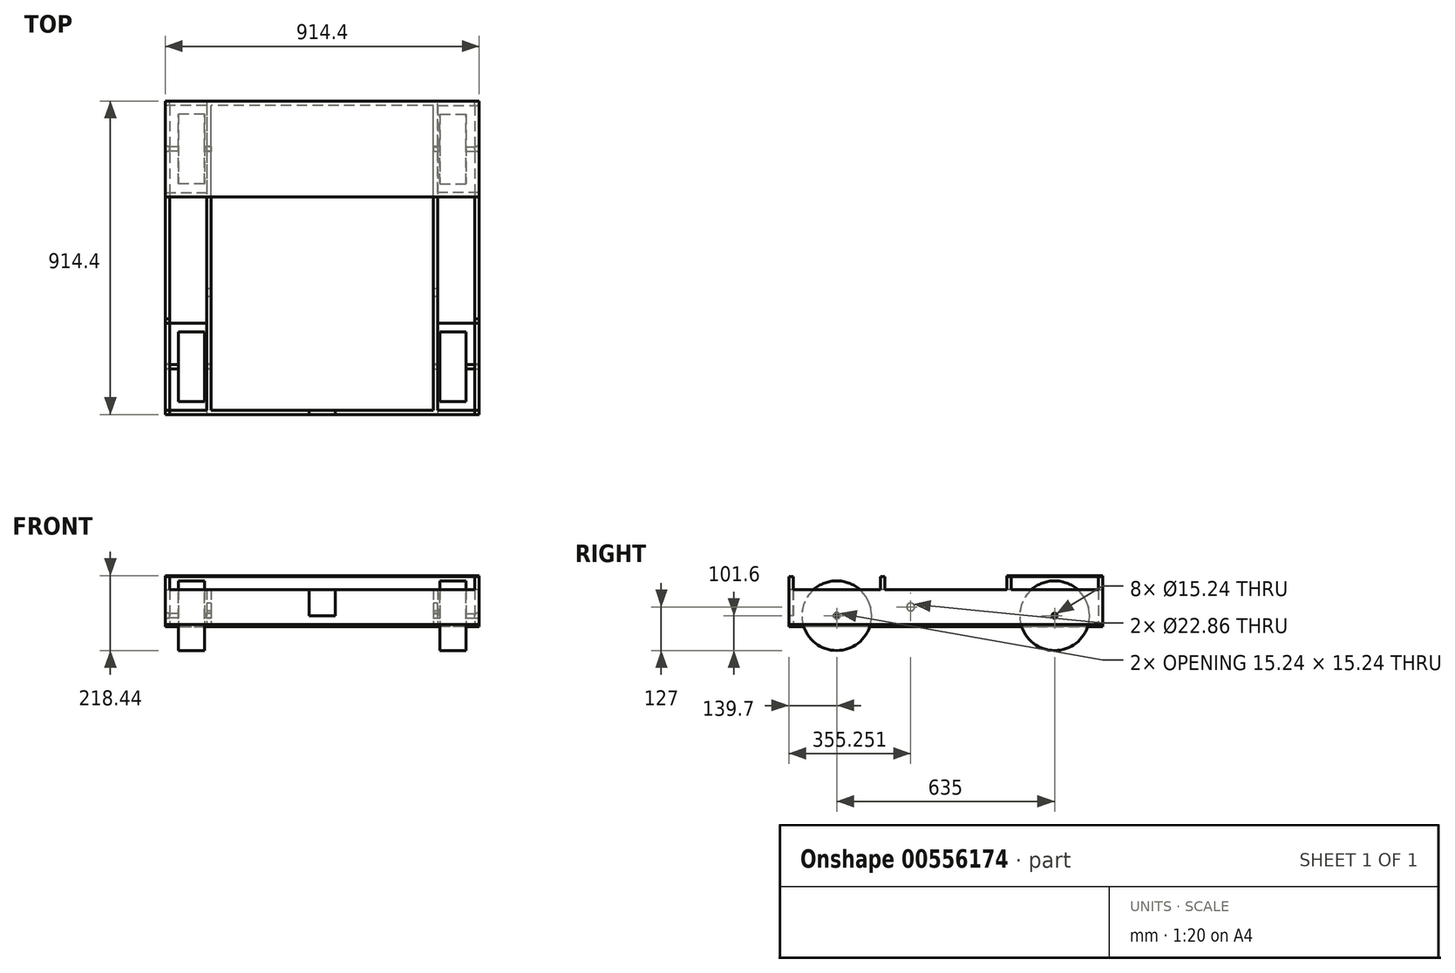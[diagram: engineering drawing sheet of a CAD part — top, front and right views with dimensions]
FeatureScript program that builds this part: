
annotation { "Feature Type Name" : "Feature", "Feature Type Description" : "" }
export const myFeature = defineFeature(function(context is Context, id is Id, definition is map)
    precondition{}
    {
        {
            var Q0;
            Q0=qCreatedBy(makeId("Top.planeOp"),FACE);
            var sketch = newSketch(context, id + "F0", { "sketchPlane" : qUnion([Q0])});
            skLineSegment(sketch, "E0", {"start": v(0, 457.2) * mm, "end": v(0, -457.2) * mm, "construction": true});
            skLineSegment(sketch, "E1", {"start": v(0, 444.5) * mm, "end": v(-444.5, 444.5) * mm});
            skLineSegment(sketch, "E2.MirrorCS", {"start": v(-254, -444.5) * mm, "end": v(-444.5, -444.5) * mm});
            skLineSegment(sketch, "E3.MirrorCS", {"start": v(0, 444.5) * mm, "end": v(444.5, 444.5) * mm});
            skLineSegment(sketch, "E4.MirrorCS", {"start": v(114.3, -444.5) * mm, "end": v(444.5, -444.5) * mm});
            skLineSegment(sketch, "E5", {"start": v(-457.2, 444.5) * mm, "end": v(-457.2, -444.5) * mm});
            skLineSegment(sketch, "E6", {"start": v(-444.5, 444.5) * mm, "end": v(-444.5, -444.5) * mm});
            skLineSegment(sketch, "E7.MirrorCS", {"start": v(444.5, 444.5) * mm, "end": v(444.5, -444.5) * mm});
            skLineSegment(sketch, "E8.MirrorCS", {"start": v(457.2, 444.5) * mm, "end": v(457.2, -444.5) * mm});
            skPoint(sketch, "E9.orphan", {"position": v(0, -444.5) * mm});
            skLineSegment(sketch, "E10.trimOffspring", {"start": v(-241.3, -457.2) * mm, "end": v(-457.2, -457.2) * mm});
            skLineSegment(sketch, "E11", {"start": v(-254, -444.5) * mm, "end": v(114.3, -444.5) * mm});
            skLineSegment(sketch, "E12", {"start": v(-38.1, -457.2) * mm, "end": v(-241.3, -457.2) * mm});
            skLineSegment(sketch, "E13", {"start": v(-457.2, 444.5) * mm, "end": v(-457.2, 457.2) * mm});
            skLineSegment(sketch, "E14", {"start": v(-457.2, -444.5) * mm, "end": v(-457.2, -457.2) * mm});
            skLineSegment(sketch, "E15", {"start": v(457.2, -444.5) * mm, "end": v(457.2, -457.2) * mm});
            skLineSegment(sketch, "E16", {"start": v(457.2, 444.5) * mm, "end": v(457.2, 457.2) * mm});
            skLineSegment(sketch, "E17.trimOffspring", {"start": v(457.2, 457.2) * mm, "end": v(-457.2, 457.2) * mm});
            skLineSegment(sketch, "E18.trimOffspring", {"start": v(457.2, -457.2) * mm, "end": v(-38.1, -457.2) * mm});
            skLineSegment(sketch, "E19", {"start": v(-336.55, 444.5) * mm, "end": v(-336.55, -444.5) * mm});
            skLineSegment(sketch, "E20", {"start": v(-323.85, -444.5) * mm, "end": v(-323.85, 444.5) * mm});
            skLineSegment(sketch, "E21.MirrorCS", {"start": v(336.55, 444.5) * mm, "end": v(336.55, -444.5) * mm});
            skLineSegment(sketch, "E22.MirrorCS", {"start": v(323.85, -444.5) * mm, "end": v(323.85, 444.5) * mm});
            skLineSegment(sketch, "E23", {"start": v(-457.2, 444.5) * mm, "end": v(-444.5, 444.5) * mm});
            skLineSegment(sketch, "E24", {"start": v(-336.55, 444.5) * mm, "end": v(-323.85, 444.5) * mm});
            skLineSegment(sketch, "E25", {"start": v(323.85, 444.5) * mm, "end": v(336.55, 444.5) * mm});
            skLineSegment(sketch, "E26", {"start": v(444.5, 444.5) * mm, "end": v(457.2, 444.5) * mm});
            skLineSegment(sketch, "E27", {"start": v(444.5, -444.5) * mm, "end": v(457.2, -444.5) * mm});
            skLineSegment(sketch, "E28", {"start": v(-444.5, -444.5) * mm, "end": v(-457.2, -444.5) * mm});
            skSolve(sketch);
        }
        {
            var Q0;
            Q0=makeQuery(id+"F0.imprint","IMPRINT",FACE,{"disambiguationData":[TD([[makeQuery(id+"F0.imprint","IMPRINT",EDGE,{"derivedFrom":sQuery(id+"F0.wireOp",EDGE,"E5")}),1.0]])]});
            var Q1;
            {var subQ0=sQuery(id+"F0.wireOp",EDGE,"E19");Q1=makeQuery(id+"F0.imprint","IMPRINT",FACE,{"disambiguationData":[TD([[makeQuery(id+"F0.imprint","IMPRINT",EDGE,{"derivedFrom":subQ0}),1.0]])]});}
            var Q2;
            Q2=makeQuery(id+"F0.imprint","IMPRINT",FACE,{"disambiguationData":[TD([[makeQuery(id+"F0.imprint","IMPRINT",EDGE,{"derivedFrom":sQuery(id+"F0.wireOp",EDGE,"E13")}),-1.0]])]});
            var Q3;
            {var subQ0=sQuery(id+"F0.wireOp",EDGE,"E21.MirrorCS");Q3=makeQuery(id+"F0.imprint","IMPRINT",FACE,{"disambiguationData":[TD([[makeQuery(id+"F0.imprint","IMPRINT",EDGE,{"derivedFrom":subQ0}),-1.0]])]});}
            var Q4;
            Q4=makeQuery(id+"F0.imprint","IMPRINT",FACE,{"disambiguationData":[TD([[makeQuery(id+"F0.imprint","IMPRINT",EDGE,{"derivedFrom":sQuery(id+"F0.wireOp",EDGE,"E7.MirrorCS")}),1.0]])]});
            var Q5;
            Q5=makeQuery(id+"F0.imprint","IMPRINT",FACE,{"disambiguationData":[TD([[makeQuery(id+"F0.imprint","IMPRINT",EDGE,{"derivedFrom":sQuery(id+"F0.wireOp",EDGE,"E10.trimOffspring")}),-1.0]])]});
            extrude(context, id + "F1", {"entities" : qUnion([Q0, Q1, Q2, Q3, Q4, Q5]), "depth" : 76.2 * mm, "offsetDistance" : 25.4 * mm, "hasSecondDirection" : true, "secondDirectionOppositeDirection" : true, "secondDirectionDepth" : 25.4 * mm});
        }
        {
            var Q0;
            Q0=makeQuery(id+"F1.opExtrude","SWEPT_FACE",FACE,{"disambiguationData":[OSD([sQuery(id+"F0.wireOp",EDGE,"E7.MirrorCS")])]});
            var sketch = newSketch(context, id + "F2", { "sketchPlane" : qUnion([Q0])});
            skLineSegment(sketch, "E29", {"start": v(-444.5, 0) * mm, "end": v(444.5, 0) * mm, "construction": true});
            skCircle(sketch, "E30", {"center": v(-317.5, 0) * mm, "radius": 7.62 * mm});
            skLineSegment(sketch, "E31", {"start": v(0, 0) * mm, "end": v(0, 76.2) * mm, "construction": true});
            skCircle(sketch, "E32.MirrorC", {"center": v(317.5, 0) * mm, "radius": 7.62 * mm});
            skSolve(sketch);
        }
        {
            var Q0;
            Q0 = qSketchRegion(id + "F2", true);
            extrude(context, id + "F3", {"entities" : qUnion([Q0]), "operationType" : NewBodyOperationType.REMOVE, "endBound" : BoundingType.THROUGH_ALL, "oppositeDirection" : true, "depth" : 38.1 * mm, "offsetDistance" : 25.4 * mm, "hasSecondDirection" : true, "secondDirectionBound" : SecondDirectionBoundingType.THROUGH_ALL, "secondDirectionOppositeDirection" : false, "secondDirectionDepth" : 25.4 * mm});
        }
        {
            var Q0;
            Q0=qCreatedBy(makeId("Top.planeOp"),FACE);
            var sketch = newSketch(context, id + "F4", { "sketchPlane" : qUnion([Q0])});
            skLineSegment(sketch, "E33.bottom", {"start": v(-419.1, 419.1) * mm, "end": v(-342.9, 419.1) * mm});
            skLineSegment(sketch, "E33.top", {"start": v(-419.1, 317.5) * mm, "end": v(-342.9, 317.5) * mm});
            skLineSegment(sketch, "E33.left", {"start": v(-419.1, 419.1) * mm, "end": v(-419.1, 317.5) * mm});
            skLineSegment(sketch, "E33.right", {"start": v(-342.9, 419.1) * mm, "end": v(-342.9, 323.85) * mm});
            skLineSegment(sketch, "E34.bottom", {"start": v(-342.9, 317.5) * mm, "end": v(-323.85, 317.5) * mm});
            skLineSegment(sketch, "E34.top", {"start": v(-342.9, 323.85) * mm, "end": v(-323.85, 323.85) * mm});
            skLineSegment(sketch, "E34.right", {"start": v(-323.85, 317.5) * mm, "end": v(-323.85, 323.85) * mm});
            skPoint(sketch, "E35", {"position": v(-323.85, 320.68) * mm});
            skLineSegment(sketch, "E36", {"start": v(-419.1, 317.5) * mm, "end": v(-457.2, 317.5) * mm});
            skLineSegment(sketch, "E37", {"start": v(-457.2, 317.5) * mm, "end": v(-457.2, 323.85) * mm});
            skLineSegment(sketch, "E38", {"start": v(-457.2, 323.85) * mm, "end": v(-419.1, 323.85) * mm});
            skLineSegment(sketch, "E39", {"start": v(-342.9, 317.5) * mm, "end": v(-342.9, 323.85) * mm});
            skLineSegment(sketch, "E40.bottom", {"start": v(-431.8, 323.85) * mm, "end": v(-425.45, 323.85) * mm});
            skLineSegment(sketch, "E40.top", {"start": v(-431.8, 342.9) * mm, "end": v(-425.45, 342.9) * mm});
            skLineSegment(sketch, "E40.left", {"start": v(-431.8, 323.85) * mm, "end": v(-431.8, 342.9) * mm});
            skLineSegment(sketch, "E40.right", {"start": v(-425.45, 323.85) * mm, "end": v(-425.45, 342.9) * mm});
            skSolve(sketch);
        }
        {
            var Q0;
            {var subQ3=sQuery(id+"F4.wireOp",EDGE,"E33.bottom");Q0=makeQuery(id+"F4.imprint","IMPRINT",FACE,{"disambiguationData":[TD([[makeQuery(id+"F4.imprint","IMPRINT",EDGE,{"derivedFrom":subQ3}),-1.0]])]});}
            var Q1;
            Q1=makeQuery(id+"F4.imprint","IMPRINT",FACE,{"disambiguationData":[TD([[makeQuery(id+"F4.imprint","IMPRINT",EDGE,{"derivedFrom":sQuery(id+"F4.wireOp",EDGE,"E34.bottom")}),1.0]])]});
            var Q2;
            {var subQ0=sQuery(id+"F4.wireOp",EDGE,"E36");Q2=makeQuery(id+"F4.imprint","IMPRINT",FACE,{"disambiguationData":[TD([[makeQuery(id+"F4.imprint","IMPRINT",EDGE,{"derivedFrom":subQ0}),-1.0]])]});}
            var Q3;
            Q3=makeQuery(id+"F4.imprint","IMPRINT",FACE,{"disambiguationData":[TD([[makeQuery(id+"F4.imprint","IMPRINT",EDGE,{"derivedFrom":sQuery(id+"F4.wireOp",EDGE,"E40.bottom")}),1.0]])]});
            var Q4;
            Q4=sQuery(id+"F4.wireOp",EDGE,"E33.top");
            revolve(context, id + "F5", {"entities" : qUnion([Q0, Q1, Q2, Q3]), "axis" : qUnion([Q4]), "revolveType" : RevolveType.FULL});
        }
        {
            var Q0;
            Q0=makeQuery(id+"F5.opRevolve","SWEPT_BODY",BODY,{"disambiguationData":[OSD([sQuery(id+"F4.wireOp",EDGE,"E33.bottom"),sQuery(id+"F4.wireOp",EDGE,"E33.top"),sQuery(id+"F4.wireOp",EDGE,"E33.left"),sQuery(id+"F4.wireOp",EDGE,"E33.right"),sQuery(id+"F4.wireOp",EDGE,"E34.bottom"),sQuery(id+"F4.wireOp",EDGE,"E34.top"),sQuery(id+"F4.wireOp",EDGE,"E34.right")])]});
            var Q1;
            Q1=qCreatedBy(makeId("Right.planeOp"),FACE);
            mirror(context, id + "F6", {"entities" : qUnion([Q0]), "mirrorPlane" : qUnion([Q1])});
        }
        {
            var Q0;
            Q0=makeQuery(id+"F5.opRevolve","SWEPT_BODY",BODY,{"disambiguationData":[OSD([sQuery(id+"F4.wireOp",EDGE,"E33.bottom"),sQuery(id+"F4.wireOp",EDGE,"E33.top"),sQuery(id+"F4.wireOp",EDGE,"E33.left"),sQuery(id+"F4.wireOp",EDGE,"E33.right"),sQuery(id+"F4.wireOp",EDGE,"E34.bottom"),sQuery(id+"F4.wireOp",EDGE,"E34.top"),sQuery(id+"F4.wireOp",EDGE,"E34.right")])]});
            var Q1;
            Q1=makeQuery(id+"F6.opPattern","COPY",BODY,{"derivedFrom":makeQuery(id+"F5.opRevolve","SWEPT_BODY",BODY,{"disambiguationData":[OSD([sQuery(id+"F4.wireOp",EDGE,"E33.bottom"),sQuery(id+"F4.wireOp",EDGE,"E33.top"),sQuery(id+"F4.wireOp",EDGE,"E33.left"),sQuery(id+"F4.wireOp",EDGE,"E33.right"),sQuery(id+"F4.wireOp",EDGE,"E34.bottom"),sQuery(id+"F4.wireOp",EDGE,"E34.top"),sQuery(id+"F4.wireOp",EDGE,"E34.right")])]}),"instanceName":"1"});
            var Q2;
            Q2=qCreatedBy(makeId("Front.planeOp"),FACE);
            mirror(context, id + "F7", {"entities" : qUnion([Q0, Q1]), "mirrorPlane" : qUnion([Q2])});
        }
        {
            var Q0;
            Q0=makeQuery(id+"F1.opExtrude","CAP_FACE",FACE,{"disambiguationData":[OSD([sQuery(id+"F0.wireOp",EDGE,"E1"),sQuery(id+"F0.wireOp",EDGE,"E2.MirrorCS"),sQuery(id+"F0.wireOp",EDGE,"E3.MirrorCS"),sQuery(id+"F0.wireOp",EDGE,"E4.MirrorCS"),sQuery(id+"F0.wireOp",EDGE,"E5"),sQuery(id+"F0.wireOp",EDGE,"E6"),sQuery(id+"F0.wireOp",EDGE,"E7.MirrorCS"),sQuery(id+"F0.wireOp",EDGE,"E8.MirrorCS"),sQuery(id+"F0.wireOp",EDGE,"E10.trimOffspring"),sQuery(id+"F0.wireOp",EDGE,"E11"),sQuery(id+"F0.wireOp",EDGE,"E12"),sQuery(id+"F0.wireOp",EDGE,"E13"),sQuery(id+"F0.wireOp",EDGE,"E14"),sQuery(id+"F0.wireOp",EDGE,"E15"),sQuery(id+"F0.wireOp",EDGE,"E16"),sQuery(id+"F0.wireOp",EDGE,"E17.trimOffspring"),sQuery(id+"F0.wireOp",EDGE,"E18.trimOffspring")])],"isStart":false});
            var sketch = newSketch(context, id + "F8", { "sketchPlane" : qUnion([Q0])});
            skLineSegment(sketch, "E41.bottom", {"start": v(-444.5, 444.5) * mm, "end": v(-457.2, 444.5) * mm});
            skLineSegment(sketch, "E41.top", {"start": v(-444.5, 457.2) * mm, "end": v(-457.2, 457.2) * mm});
            skLineSegment(sketch, "E41.left", {"start": v(-444.5, 444.5) * mm, "end": v(-444.5, 457.2) * mm});
            skLineSegment(sketch, "E41.right", {"start": v(-457.2, 444.5) * mm, "end": v(-457.2, 457.2) * mm});
            skLineSegment(sketch, "E42", {"start": v(-444.5, 0) * mm, "end": v(444.5, 0) * mm, "construction": true});
            skLineSegment(sketch, "E43", {"start": v(-457.2, 444.5) * mm, "end": v(-457.2, 0) * mm, "construction": true});
            skLineSegment(sketch, "E44.bottom", {"start": v(-457.2, 190.5) * mm, "end": v(-444.5, 190.5) * mm});
            skLineSegment(sketch, "E44.top", {"start": v(-457.2, 177.8) * mm, "end": v(-444.5, 177.8) * mm});
            skLineSegment(sketch, "E44.left", {"start": v(-457.2, 190.5) * mm, "end": v(-457.2, 177.8) * mm});
            skLineSegment(sketch, "E44.right", {"start": v(-444.5, 190.5) * mm, "end": v(-444.5, 177.8) * mm});
            skLineSegment(sketch, "E45.MirrorCS", {"start": v(457.2, 444.5) * mm, "end": v(457.2, 457.2) * mm});
            skLineSegment(sketch, "E46.MirrorCS", {"start": v(444.5, 444.5) * mm, "end": v(444.5, 457.2) * mm});
            skLineSegment(sketch, "E47.MirrorCS", {"start": v(444.5, 457.2) * mm, "end": v(457.2, 457.2) * mm});
            skLineSegment(sketch, "E48.MirrorCS", {"start": v(444.5, 444.5) * mm, "end": v(457.2, 444.5) * mm});
            skLineSegment(sketch, "E49.MirrorCS", {"start": v(457.2, 190.5) * mm, "end": v(444.5, 190.5) * mm});
            skLineSegment(sketch, "E50.MirrorCS", {"start": v(457.2, 177.8) * mm, "end": v(444.5, 177.8) * mm});
            skLineSegment(sketch, "E51.MirrorCS", {"start": v(444.5, 190.5) * mm, "end": v(444.5, 177.8) * mm});
            skLineSegment(sketch, "E52.MirrorCS", {"start": v(457.2, 190.5) * mm, "end": v(457.2, 177.8) * mm});
            skLineSegment(sketch, "E53.MirrorCS", {"start": v(444.5, -444.5) * mm, "end": v(457.2, -444.5) * mm});
            skLineSegment(sketch, "E54.MirrorCS", {"start": v(-444.5, -444.5) * mm, "end": v(-457.2, -444.5) * mm});
            skLineSegment(sketch, "E55.MirrorCS", {"start": v(-444.5, -457.2) * mm, "end": v(-457.2, -457.2) * mm});
            skLineSegment(sketch, "E56.MirrorCS", {"start": v(-444.5, -444.5) * mm, "end": v(-444.5, -457.2) * mm});
            skLineSegment(sketch, "E57.MirrorCS", {"start": v(-457.2, -444.5) * mm, "end": v(-457.2, -457.2) * mm});
            skLineSegment(sketch, "E58.MirrorCS", {"start": v(457.2, -444.5) * mm, "end": v(457.2, -457.2) * mm});
            skLineSegment(sketch, "E59.MirrorCS", {"start": v(444.5, -444.5) * mm, "end": v(444.5, -457.2) * mm});
            skLineSegment(sketch, "E60.MirrorCS", {"start": v(457.2, -190.5) * mm, "end": v(444.5, -190.5) * mm});
            skLineSegment(sketch, "E61.MirrorCS", {"start": v(457.2, -177.8) * mm, "end": v(444.5, -177.8) * mm});
            skLineSegment(sketch, "E62.MirrorCS", {"start": v(444.5, -190.5) * mm, "end": v(444.5, -177.8) * mm});
            skLineSegment(sketch, "E63.MirrorCS", {"start": v(457.2, -190.5) * mm, "end": v(457.2, -177.8) * mm});
            skLineSegment(sketch, "E64.MirrorCS", {"start": v(-457.2, -190.5) * mm, "end": v(-444.5, -190.5) * mm});
            skLineSegment(sketch, "E65.MirrorCS", {"start": v(-444.5, -190.5) * mm, "end": v(-444.5, -177.8) * mm});
            skLineSegment(sketch, "E66.MirrorCS", {"start": v(-457.2, -177.8) * mm, "end": v(-444.5, -177.8) * mm});
            skLineSegment(sketch, "E67.MirrorCS", {"start": v(-457.2, -190.5) * mm, "end": v(-457.2, -177.8) * mm});
            skLineSegment(sketch, "E68.MirrorCS", {"start": v(444.5, -457.2) * mm, "end": v(457.2, -457.2) * mm});
            skSolve(sketch);
        }
        {
            var Q0;
            Q0 = qSketchRegion(id + "F8", true);
            extrude(context, id + "F9", {"entities" : qUnion([Q0]), "operationType" : NewBodyOperationType.ADD, "depth" : 38.1 * mm, "offsetDistance" : 25.4 * mm});
        }
        {
            var Q0;
            Q0=makeQuery(id+"F9.opExtrude","CAP_FACE",FACE,{"disambiguationData":[OSD([sQuery(id+"F8.wireOp",EDGE,"E41.bottom"),sQuery(id+"F8.wireOp",EDGE,"E41.top"),sQuery(id+"F8.wireOp",EDGE,"E41.left"),sQuery(id+"F8.wireOp",EDGE,"E41.right")])],"isStart":false});
            var sketch = newSketch(context, id + "F10", { "sketchPlane" : qUnion([Q0])});
            skLineSegment(sketch, "E69.bottom", {"start": v(-457.2, 457.2) * mm, "end": v(457.2, 457.2) * mm});
            skLineSegment(sketch, "E69.top", {"start": v(-457.2, 177.8) * mm, "end": v(457.2, 177.8) * mm});
            skLineSegment(sketch, "E69.left", {"start": v(-457.2, 457.2) * mm, "end": v(-457.2, 177.8) * mm});
            skLineSegment(sketch, "E69.right", {"start": v(457.2, 457.2) * mm, "end": v(457.2, 177.8) * mm});
            skSolve(sketch);
        }
        {
            var Q0;
            Q0 = qSketchRegion(id + "F10", true);
            extrude(context, id + "F11", {"entities" : qUnion([Q0]), "depth" : 2.54 * mm, "offsetDistance" : 25.4 * mm});
        }
        {
            var Q0;
            Q0=makeQuery(id+"F1.opExtrude","CAP_FACE",FACE,{"disambiguationData":[OSD([sQuery(id+"F0.wireOp",EDGE,"QB7noLBN-PpOc-EJPR-Sd6c-0ypbwZ1Wte7m.bottom"),sQuery(id+"F0.wireOp",EDGE,"QB7noLBN-PpOc-EJPR-Sd6c-0ypbwZ1Wte7m.top"),sQuery(id+"F0.wireOp",EDGE,"QB7noLBN-PpOc-EJPR-Sd6c-0ypbwZ1Wte7m.left"),sQuery(id+"F0.wireOp",EDGE,"QB7noLBN-PpOc-EJPR-Sd6c-0ypbwZ1Wte7m.right"),sQuery(id+"F0.wireOp",EDGE,"PR4ij4Z3-PY9W-TKVm-yz0G-q3J5sclFM2MW"),sQuery(id+"F0.wireOp",EDGE,"E1"),sQuery(id+"F0.wireOp",EDGE,"E2.MirrorCS"),sQuery(id+"F0.wireOp",EDGE,"E3.MirrorCS"),sQuery(id+"F0.wireOp",EDGE,"855b87ce-e732-4e19-91af-ca48fbd712201.MirrorCS"),sQuery(id+"F0.wireOp",EDGE,"E4.MirrorCS"),sQuery(id+"F0.wireOp",EDGE,"E5"),sQuery(id+"F0.wireOp",EDGE,"E6"),sQuery(id+"F0.wireOp",EDGE,"E7.MirrorCS"),sQuery(id+"F0.wireOp",EDGE,"E8.MirrorCS"),sQuery(id+"F0.wireOp",EDGE,"31cbcaf3-3368-42d4-bf1a-20ab076e13b5.trimOffspring"),sQuery(id+"F0.wireOp",EDGE,"ae03b67a-2540-4bec-9181-0f3f2fe8d185.trimOffspring"),sQuery(id+"F0.wireOp",EDGE,"7d0354b2-750d-4ba2-8c9c-4a323621a8be.trimOffspring"),sQuery(id+"F0.wireOp",EDGE,"423b36b6-17ea-44a3-93c2-e0b44851f98a.trimOffspring"),sQuery(id+"F0.wireOp",EDGE,"E10.trimOffspring"),sQuery(id+"F0.wireOp",EDGE,"E11"),sQuery(id+"F0.wireOp",EDGE,"E12")])],"isStart":true});
            var sketch = newSketch(context, id + "F12", { "sketchPlane" : qUnion([Q0])});
            skLineSegment(sketch, "E70", {"start": v(0, -457.2) * mm, "end": v(0, 457.2) * mm, "construction": true});
            skLineSegment(sketch, "E71", {"start": v(-457.2, 0) * mm, "end": v(457.2, 0) * mm, "construction": true});
            skLineSegment(sketch, "E72", {"start": v(-457.2, 0) * mm, "end": v(-457.2, 190.5) * mm});
            skLineSegment(sketch, "E73", {"start": v(-457.2, 190.5) * mm, "end": v(-336.55, 190.5) * mm});
            skLineSegment(sketch, "E74", {"start": v(-336.55, 190.5) * mm, "end": v(-336.55, 457.2) * mm});
            skLineSegment(sketch, "E75", {"start": v(-336.55, 457.2) * mm, "end": v(0, 457.2) * mm});
            skLineSegment(sketch, "E76.MirrorCS", {"start": v(336.55, 457.2) * mm, "end": v(0, 457.2) * mm});
            skLineSegment(sketch, "E77.MirrorCS", {"start": v(457.2, 0) * mm, "end": v(457.2, 190.5) * mm});
            skLineSegment(sketch, "E78.MirrorCS", {"start": v(457.2, 190.5) * mm, "end": v(336.55, 190.5) * mm});
            skLineSegment(sketch, "E79.MirrorCS", {"start": v(336.55, 190.5) * mm, "end": v(336.55, 457.2) * mm});
            skLineSegment(sketch, "E80.MirrorCS", {"start": v(457.2, -190.5) * mm, "end": v(336.55, -190.5) * mm});
            skLineSegment(sketch, "E81.MirrorCS", {"start": v(336.55, -190.5) * mm, "end": v(336.55, -457.2) * mm});
            skLineSegment(sketch, "E82.MirrorCS", {"start": v(457.2, 0) * mm, "end": v(457.2, -190.5) * mm});
            skLineSegment(sketch, "E83.MirrorCS", {"start": v(336.55, -457.2) * mm, "end": v(0, -457.2) * mm});
            skLineSegment(sketch, "E84.MirrorCS", {"start": v(-336.55, -457.2) * mm, "end": v(0, -457.2) * mm});
            skLineSegment(sketch, "E85.MirrorCS", {"start": v(-336.55, -190.5) * mm, "end": v(-336.55, -457.2) * mm});
            skLineSegment(sketch, "E86.MirrorCS", {"start": v(-457.2, -190.5) * mm, "end": v(-336.55, -190.5) * mm});
            skLineSegment(sketch, "E87.MirrorCS", {"start": v(-457.2, 0) * mm, "end": v(-457.2, -190.5) * mm});
            skSolve(sketch);
        }
        {
            var Q0;
            Q0 = qSketchRegion(id + "F12", true);
            extrude(context, id + "F13", {"entities" : qUnion([Q0]), "depth" : 6.35 * mm, "offsetDistance" : 25.4 * mm});
        }
        {
            var Q0;
            Q0=makeQuery(id+"F1.opExtrude","SWEPT_FACE",FACE,{"disambiguationData":[OSD([sQuery(id+"F0.wireOp",EDGE,"E19")])]});
            var sketch = newSketch(context, id + "F14", { "sketchPlane" : qUnion([Q0])});
            skCircle(sketch, "E88", {"center": v(101.95, 25.4) * mm, "radius": 11.43 * mm});
            skSolve(sketch);
        }
        {
            var Q0;
            Q0 = qSketchRegion(id + "F14", true);
            extrude(context, id + "F15", {"entities" : qUnion([Q0]), "operationType" : NewBodyOperationType.REMOVE, "oppositeDirection" : true, "depth" : 762 * mm, "offsetDistance" : 25.4 * mm});
        }
        {
            var Q0;
            Q0=makeQuery(id+"F9.boolean.opBoolean","MERGE",FACE,{"derivedFrom":[makeQuery(id+"F1.opExtrude","SWEPT_FACE",FACE,{"disambiguationData":[OSD([sQuery(id+"F0.wireOp",EDGE,"E10.trimOffspring"),sQuery(id+"F0.wireOp",EDGE,"E12"),sQuery(id+"F0.wireOp",EDGE,"E18.trimOffspring")])]}),makeQuery(id+"F9.opExtrude","SWEPT_FACE",FACE,{"disambiguationData":[OSD([sQuery(id+"F8.wireOp",EDGE,"E55.MirrorCS")])]}),makeQuery(id+"F9.opExtrude","SWEPT_FACE",FACE,{"disambiguationData":[OSD([sQuery(id+"F8.wireOp",EDGE,"E68.MirrorCS")])]})]});
            var sketch = newSketch(context, id + "F16", { "sketchPlane" : qUnion([Q0])});
            skLineSegment(sketch, "E89", {"start": v(-457.2, -25.4) * mm, "end": v(457.2, -25.4) * mm, "construction": true});
            skLineSegment(sketch, "E90", {"start": v(0, -25.4) * mm, "end": v(0, 76.2) * mm, "construction": true});
            skLineSegment(sketch, "E91.bottom", {"start": v(38.1, 76.2) * mm, "end": v(-38.1, 76.2) * mm});
            skLineSegment(sketch, "E91.top", {"start": v(38.1, -25.4) * mm, "end": v(-38.1, -25.4) * mm});
            skLineSegment(sketch, "E91.left", {"start": v(38.1, 76.2) * mm, "end": v(38.1, 0) * mm});
            skLineSegment(sketch, "E91.right", {"start": v(-38.1, 76.2) * mm, "end": v(-38.1, 0) * mm});
            skPoint(sketch, "E91.middle", {"position": v(0, 25.4) * mm});
            skLineSegment(sketch, "E92", {"start": v(-38.1, 0) * mm, "end": v(38.1, 0) * mm});
            skSolve(sketch);
        }
        {
            var Q0;
            Q0 = qSketchRegion(id + "F16", true);
            extrude(context, id + "F17", {"entities" : qUnion([Q0]), "operationType" : NewBodyOperationType.REMOVE, "oppositeDirection" : true, "depth" : 25.4 * mm, "offsetDistance" : 25.4 * mm});
        }
    });
